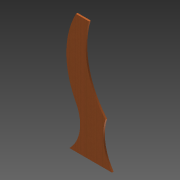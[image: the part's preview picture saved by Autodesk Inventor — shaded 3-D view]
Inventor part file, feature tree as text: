
AUTODESK INVENTOR PART (.ipt)
format: ipt  version: 2013 (Build 170138000, 138)  size: 86,016 bytes
history: native  units: in
note: dims shown in document units (in); Inventor stores cm internally (conversion verified against a paired STEP export)
features: extrude x1, sketch x1
ambient origin geometry x8: Origin, YZ Plane, XZ Plane, XY Plane, X Axis, Y Axis, Z Axis, Center Point
bodies: Solid1 (feature_tree)
feature tree (2):
  extrude  "Extrusion1"  Depth=48.0in
  sketch  "Sketch1"  dims[d0=18.0in d1=48.0in d2=50.0in d5=26.0in d6=26.0in d7=30.0in d8=1.0in d9=0.0in d10=8.0in]
